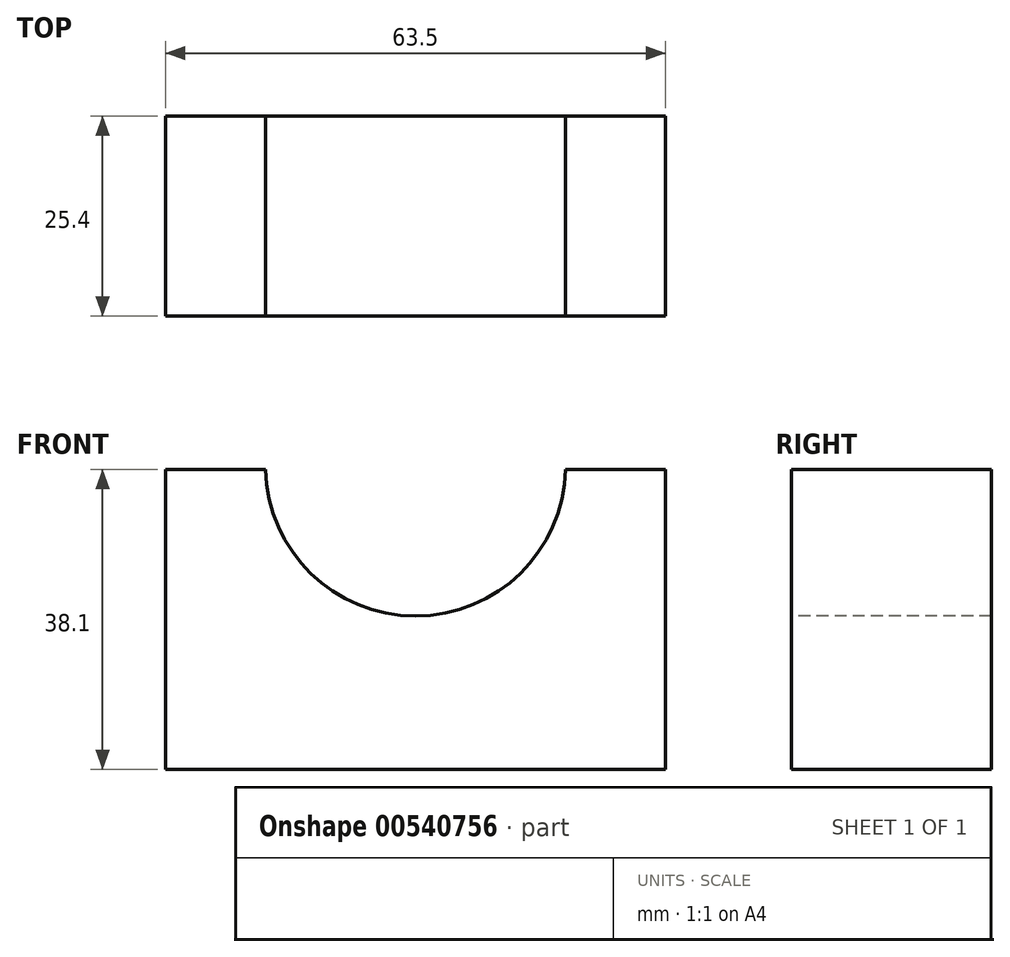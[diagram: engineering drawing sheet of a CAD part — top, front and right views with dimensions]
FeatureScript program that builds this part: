
annotation { "Feature Type Name" : "Feature", "Feature Type Description" : "" }
export const myFeature = defineFeature(function(context is Context, id is Id, definition is map)
    precondition{}
    {
        {
            var Q0;
            Q0=qCreatedBy(makeId("Front.planeOp"),FACE);
            var sketch = newSketch(context, id + "F0", { "sketchPlane" : qUnion([Q0])});
            skLineSegment(sketch, "E0", {"start": v(0, 0) * mm, "end": v(63.5, 0) * mm});
            skLineSegment(sketch, "E1", {"start": v(63.5, 0) * mm, "end": v(63.5, 38.1) * mm});
            skLineSegment(sketch, "E2", {"start": v(63.5, 38.1) * mm, "end": v(0, 38.1) * mm});
            skLineSegment(sketch, "E3", {"start": v(0, 38.1) * mm, "end": v(0, 0) * mm});
            skSolve(sketch);
        }
        {
            var Q0;
            Q0=makeQuery(id+"F0.imprint","IMPRINT",FACE,{"disambiguationData":[TD([[makeQuery(id+"F0.imprint","IMPRINT",EDGE,{"derivedFrom":sQuery(id+"F0.wireOp",EDGE,"E0")}),1.0]])]});
            extrude(context, id + "F1", {"entities" : qUnion([Q0]), "depth" : 25.4 * mm, "offsetDistance" : 25.4 * mm});
        }
        {
            var Q0;
            Q0=makeQuery(id+"F1.opExtrude","CAP_FACE",FACE,{"disambiguationData":[OSD([sQuery(id+"F0.wireOp",EDGE,"E0"),sQuery(id+"F0.wireOp",EDGE,"E1"),sQuery(id+"F0.wireOp",EDGE,"E2"),sQuery(id+"F0.wireOp",EDGE,"E3")])],"isStart":false});
            var sketch = newSketch(context, id + "F2", { "sketchPlane" : qUnion([Q0])});
            skCircle(sketch, "E4", {"center": v(31.75, 38.53) * mm, "radius": 19.05 * mm});
            skSolve(sketch);
        }
        {
            var Q0;
            Q0=makeQuery(id+"F2.imprint","IMPRINT",FACE,{"disambiguationData":[TD([[makeQuery(id+"F2.imprint","IMPRINT",EDGE,{"derivedFrom":sQuery(id+"F2.wireOp",EDGE,"E4")}),1.0]])]});
            extrude(context, id + "F3", {"entities" : qUnion([Q0]), "operationType" : NewBodyOperationType.REMOVE, "oppositeDirection" : true, "depth" : 25.4 * mm, "offsetDistance" : 25.4 * mm});
        }
    });
